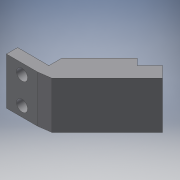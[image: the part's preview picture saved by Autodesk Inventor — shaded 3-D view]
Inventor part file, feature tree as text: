
AUTODESK INVENTOR PART (.ipt)
format: ipt  version: 2017 SP1 (Build 210196100, 196)  size: 178,176 bytes
history: native  units: mm
features: extrude x5, sketch x5, projected_geometry x3
ambient origin geometry x8: Origin, YZ Plane, XZ Plane, XY Plane, X Axis, Y Axis, Z Axis, Center Point
bodies: Solid1 (feature_tree)
feature tree (13):
  extrude  "Extrusion1"  Depth=31.0mm
  extrude  "Extrusion2"  Depth=14.0mm
  sketch  "Sketch3"  dims[d5=2.0mm d6=2.0mm]
  extrude  "Extrusion3"  Depth=2.0mm
  extrude  "Extrusion4"  Depth=4.0mm
  extrude  "Extrusion5"  Depth=21.0mm TaperAngle=0.0deg
  sketch  "Sketch1"  dims[d0=19.0mm d1=31.0mm]
  sketch  "Sketch2"  dims[d2=14.0mm d4=60.0mm]
  projected_geometry  "Projected Loop1"
  sketch  "Sketch4"  dims[d8=4.0mm d9=35.0mm]
  projected_geometry  "Projected Loop2"
  sketch  "Sketch5"  dims[d10=45.0deg d11=21.0mm d12=0.0mm d13=5.0mm d14=17.0mm d15=20.0mm d16=5.0mm d17=0.0mm d18=6.0mm d19=8.0mm d20=4.0mm d21=17.0mm d22=0.0mm d23=17.0mm d24=0.0mm d25=5.0mm d26=12.0mm d27=17.0mm d28=0.0mm]
  projected_geometry  "Projected Loop3"
